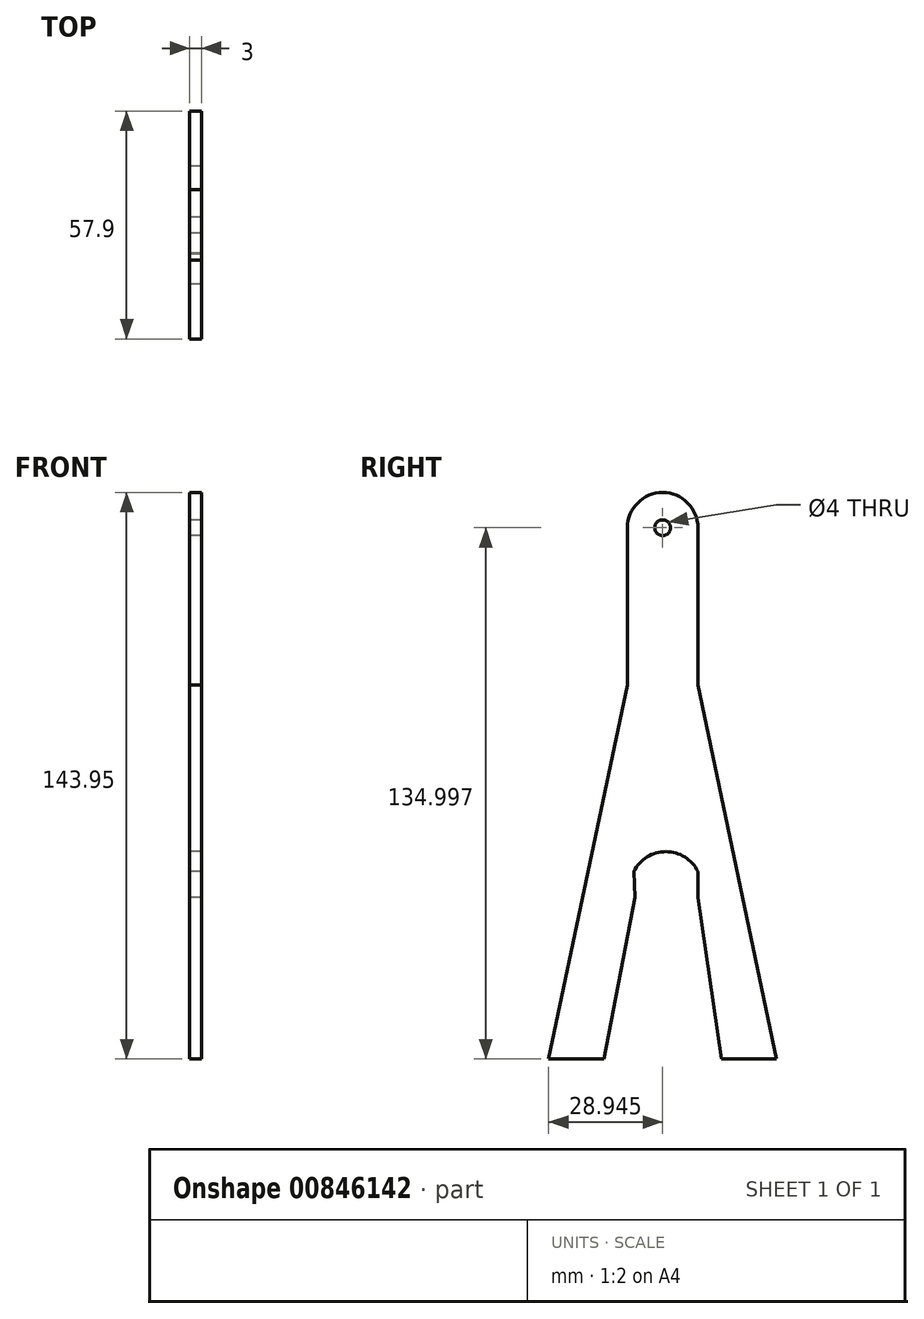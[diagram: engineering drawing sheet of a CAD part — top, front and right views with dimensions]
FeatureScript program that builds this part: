
annotation { "Feature Type Name" : "Feature", "Feature Type Description" : "" }
export const myFeature = defineFeature(function(context is Context, id is Id, definition is map)
    precondition{}
    {
        {
            var Q0;
            Q0=qCreatedBy(makeId("Right.planeOp"),FACE);
            var sketch = newSketch(context, id + "F0", { "sketchPlane" : qUnion([Q0])});
            skLineSegment(sketch, "E0", {"start": v(-10.58, 93.38) * mm, "end": v(-10.58, 53.38) * mm});
            skLineSegment(sketch, "E1", {"start": v(7.32, 93.38) * mm, "end": v(7.32, 53.38) * mm});
            skArc(sketch, "E2", {"start": v(7.32, 93.38) * mm, "mid": v(-1.63, 102.33) * mm, "end": v(-10.58, 93.38) * mm});
            skLineSegment(sketch, "E3", {"start": v(-10.58, 53.38) * mm, "end": v(-30.58, -41.62) * mm});
            skLineSegment(sketch, "E4", {"start": v(-30.58, -41.62) * mm, "end": v(-16.58, -41.62) * mm});
            skLineSegment(sketch, "E5", {"start": v(-16.58, -41.62) * mm, "end": v(-8.72, -0.51) * mm});
            skLineSegment(sketch, "E6", {"start": v(7.32, -0.51) * mm, "end": v(13.32, -41.62) * mm});
            skLineSegment(sketch, "E7", {"start": v(13.32, -41.62) * mm, "end": v(27.32, -41.62) * mm});
            skLineSegment(sketch, "E8", {"start": v(7.32, 53.38) * mm, "end": v(27.32, -41.62) * mm});
            skArc(sketch, "E9", {"start": v(7.32, 6.05) * mm, "mid": v(-0.82, 11.09) * mm, "end": v(-8.95, 6.05) * mm});
            skLineSegment(sketch, "E10", {"start": v(7.32, -0.51) * mm, "end": v(7.32, 6.05) * mm});
            skLineSegment(sketch, "E11", {"start": v(-8.95, 6.05) * mm, "end": v(-8.72, -0.51) * mm});
            skCircle(sketch, "E12", {"center": v(-1.63, 93.38) * mm, "radius": 2 * mm});
            skSolve(sketch);
        }
        {
            var Q0;
            Q0=makeQuery(id+"F0.imprint","IMPRINT",FACE,{"disambiguationData":[TD([[makeQuery(id+"F0.imprint","IMPRINT",EDGE,{"derivedFrom":sQuery(id+"F0.wireOp",EDGE,"E0")}),1.0]])]});
            var sketch = newSketch(context, id + "F1", { "sketchPlane" : qUnion([Q0])});
            skSolve(sketch);
        }
        {
            var Q0;
            Q0=makeQuery(id+"F1.imprint","IMPRINT",FACE,{"disambiguationData":[TD([[makeQuery(id+"F1.imprint","IMPRINT",EDGE,{"derivedFrom":makeQuery(id+"F0.imprint","IMPRINT",EDGE,{"derivedFrom":sQuery(id+"F0.wireOp",EDGE,"E0")})}),1.0]])]});
            extrude(context, id + "F2", {"entities" : qUnion([Q0]), "depth" : 3 * mm, "offsetDistance" : 25 * mm});
        }
    });
